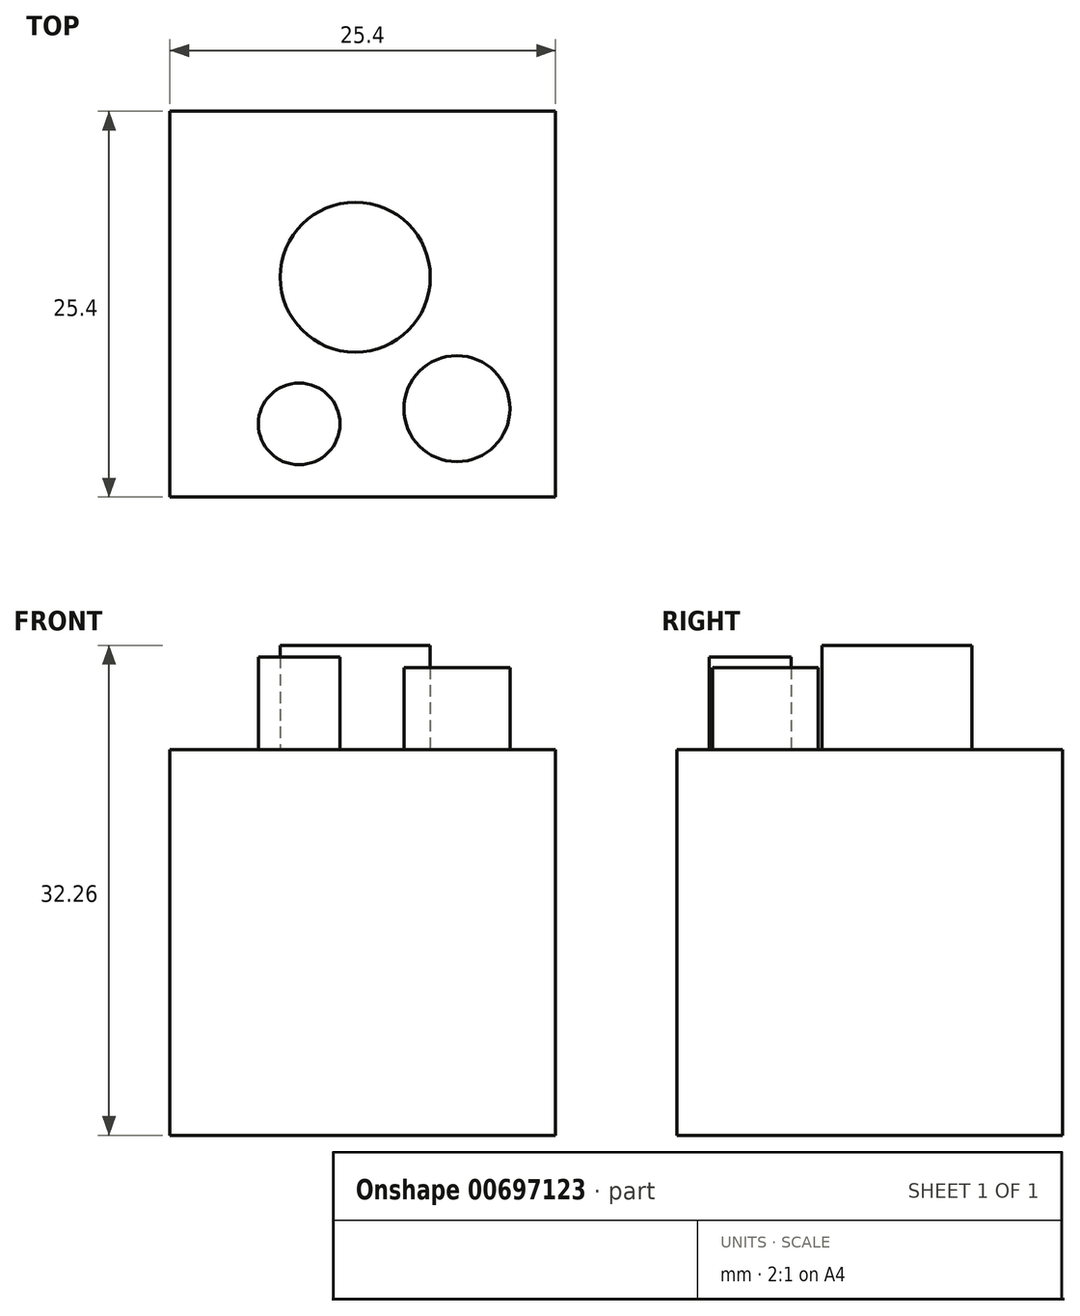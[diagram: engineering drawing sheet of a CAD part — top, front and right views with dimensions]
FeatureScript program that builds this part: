
annotation { "Feature Type Name" : "Feature", "Feature Type Description" : "" }
export const myFeature = defineFeature(function(context is Context, id is Id, definition is map)
    precondition{}
    {
        {
            var Q0;
            Q0=qCreatedBy(makeId("Front.planeOp"),FACE);
            var sketch = newSketch(context, id + "F0", { "sketchPlane" : qUnion([Q0])});
            skLineSegment(sketch, "E0.bottom", {"start": v(-12.2, 11.9) * mm, "end": v(13.2, 11.9) * mm});
            skLineSegment(sketch, "E0.top", {"start": v(-12.2, -13.5) * mm, "end": v(13.2, -13.5) * mm});
            skLineSegment(sketch, "E0.left", {"start": v(-12.2, 11.9) * mm, "end": v(-12.2, -13.5) * mm});
            skLineSegment(sketch, "E0.right", {"start": v(13.2, 11.9) * mm, "end": v(13.2, -13.5) * mm});
            skSolve(sketch);
        }
        {
            var Q0;
            Q0 = qSketchRegion(id + "F0", true);
            extrude(context, id + "F1", {"entities" : qUnion([Q0]), "depth" : 25.4 * mm, "offsetDistance" : 25.4 * mm});
        }
        {
            var Q0;
            Q0=makeQuery(id+"F1.opExtrude","SWEPT_FACE",FACE,{"disambiguationData":[OSD([sQuery(id+"F0.wireOp",EDGE,"E0.bottom")])]});
            var sketch = newSketch(context, id + "F2", { "sketchPlane" : qUnion([Q0])});
            skCircle(sketch, "E1", {"center": v(0, -10.92) * mm, "radius": 4.94 * mm});
            skSolve(sketch);
        }
        {
            var Q0;
            Q0 = qSketchRegion(id + "F2", true);
            extrude(context, id + "F3", {"entities" : qUnion([Q0]), "operationType" : NewBodyOperationType.ADD, "depth" : 6.86 * mm, "offsetDistance" : 25.4 * mm});
        }
        {
            var Q0;
            Q0=makeQuery(id+"F1.opExtrude","SWEPT_FACE",FACE,{"disambiguationData":[OSD([sQuery(id+"F0.wireOp",EDGE,"E0.bottom")])]});
            var sketch = newSketch(context, id + "F4", { "sketchPlane" : qUnion([Q0])});
            skCircle(sketch, "E2", {"center": v(-3.7, -20.58) * mm, "radius": 2.69 * mm});
            skSolve(sketch);
        }
        {
            var Q0;
            Q0 = qSketchRegion(id + "F4", true);
            extrude(context, id + "F5", {"entities" : qUnion([Q0]), "operationType" : NewBodyOperationType.ADD, "depth" : 6.1 * mm, "offsetDistance" : 25.4 * mm});
        }
        {
            var Q0;
            Q0=makeQuery(id+"F1.opExtrude","SWEPT_FACE",FACE,{"disambiguationData":[OSD([sQuery(id+"F0.wireOp",EDGE,"E0.bottom")])]});
            var sketch = newSketch(context, id + "F6", { "sketchPlane" : qUnion([Q0])});
            skCircle(sketch, "E3", {"center": v(6.7, -19.58) * mm, "radius": 3.49 * mm});
            skSolve(sketch);
        }
        {
            var Q0;
            Q0 = qSketchRegion(id + "F6", true);
            extrude(context, id + "F7", {"entities" : qUnion([Q0]), "operationType" : NewBodyOperationType.ADD, "depth" : 5.38 * mm, "offsetDistance" : 25.4 * mm});
        }
    });
